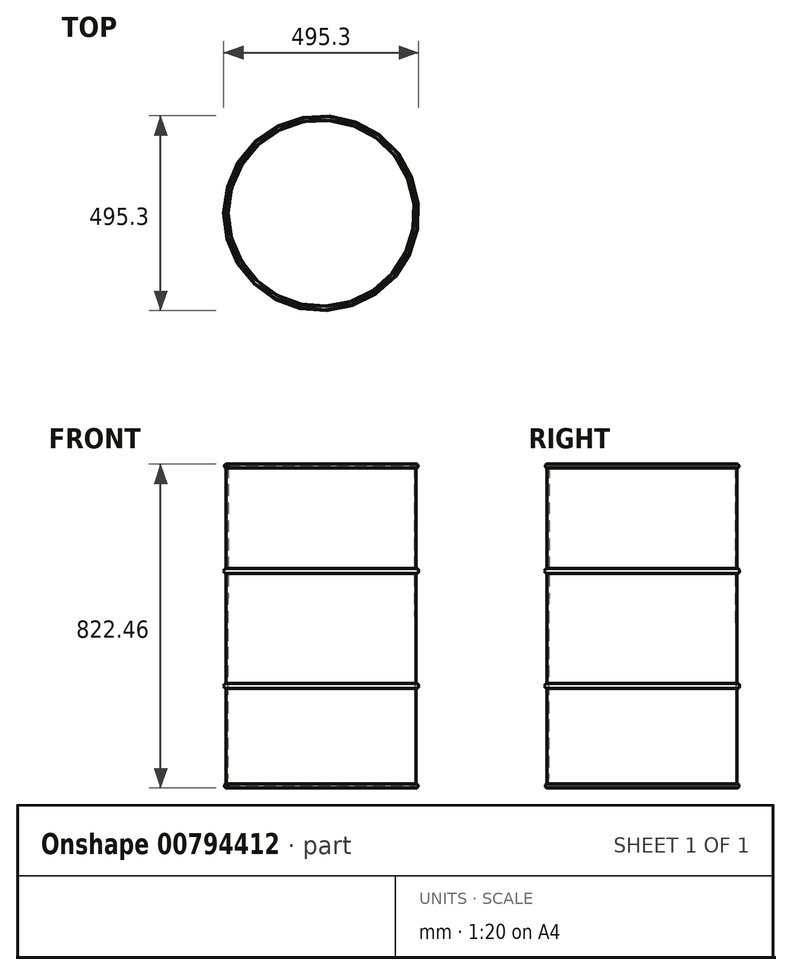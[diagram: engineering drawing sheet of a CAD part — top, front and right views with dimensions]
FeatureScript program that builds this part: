
annotation { "Feature Type Name" : "Feature", "Feature Type Description" : "" }
export const myFeature = defineFeature(function(context is Context, id is Id, definition is map)
    precondition{}
    {
        {
            var Q0;
            Q0=qCreatedBy(makeId("Front.planeOp"),FACE);
            var sketch = newSketch(context, id + "F0", { "sketchPlane" : qUnion([Q0])});
            skLineSegment(sketch, "E0", {"start": v(0, 0) * mm, "end": v(0, 812.8) * mm});
            skLineSegment(sketch, "E1.0", {"start": v(241.3, 4.83) * mm, "end": v(241.3, 247.65) * mm});
            skLineSegment(sketch, "E2", {"start": v(0, 0) * mm, "end": v(236.47, 0) * mm});
            skArc(sketch, "E3", {"start": v(241.3, 807.97) * mm, "mid": v(244.63, 816.3) * mm, "end": v(236.48, 812.56) * mm});
            skArc(sketch, "E4", {"start": v(241.3, 539.75) * mm, "mid": v(247.65, 546.1) * mm, "end": v(241.3, 552.45) * mm});
            skArc(sketch, "E5", {"start": v(241.3, 247.65) * mm, "mid": v(247.65, 254) * mm, "end": v(241.3, 260.35) * mm});
            skLineSegment(sketch, "E6.trimOffspring", {"start": v(241.3, 552.45) * mm, "end": v(241.3, 807.97) * mm});
            skLineSegment(sketch, "E7.trimOffspring", {"start": v(241.3, 260.35) * mm, "end": v(241.3, 539.75) * mm});
            skArc(sketch, "E8", {"start": v(236.47, 0) * mm, "mid": v(244.71, -3.41) * mm, "end": v(241.3, 4.83) * mm});
            skLineSegment(sketch, "E9", {"start": v(236.48, 813.01) * mm, "end": v(238.73, 4.83) * mm});
            skLineSegment(sketch, "E10", {"start": v(238.73, 4.83) * mm, "end": v(0, 4.16) * mm});
            skLineSegment(sketch, "E11", {"start": v(0, 4.16) * mm, "end": v(0, 0) * mm});
            skSolve(sketch);
        }
        {
            var Q0;
            Q0=qSketchRegion(id+"F0",true);
            var Q1;
            Q1=sQuery(id+"F0.wireOp",EDGE,"E0");
            revolve(context, id + "F1", {"surfaceOperationType" : NewSurfaceOperationType.NEW, "entities" : qUnion([Q0]), "axis" : qUnion([Q1]), "revolveType" : RevolveType.FULL});
        }
    });
